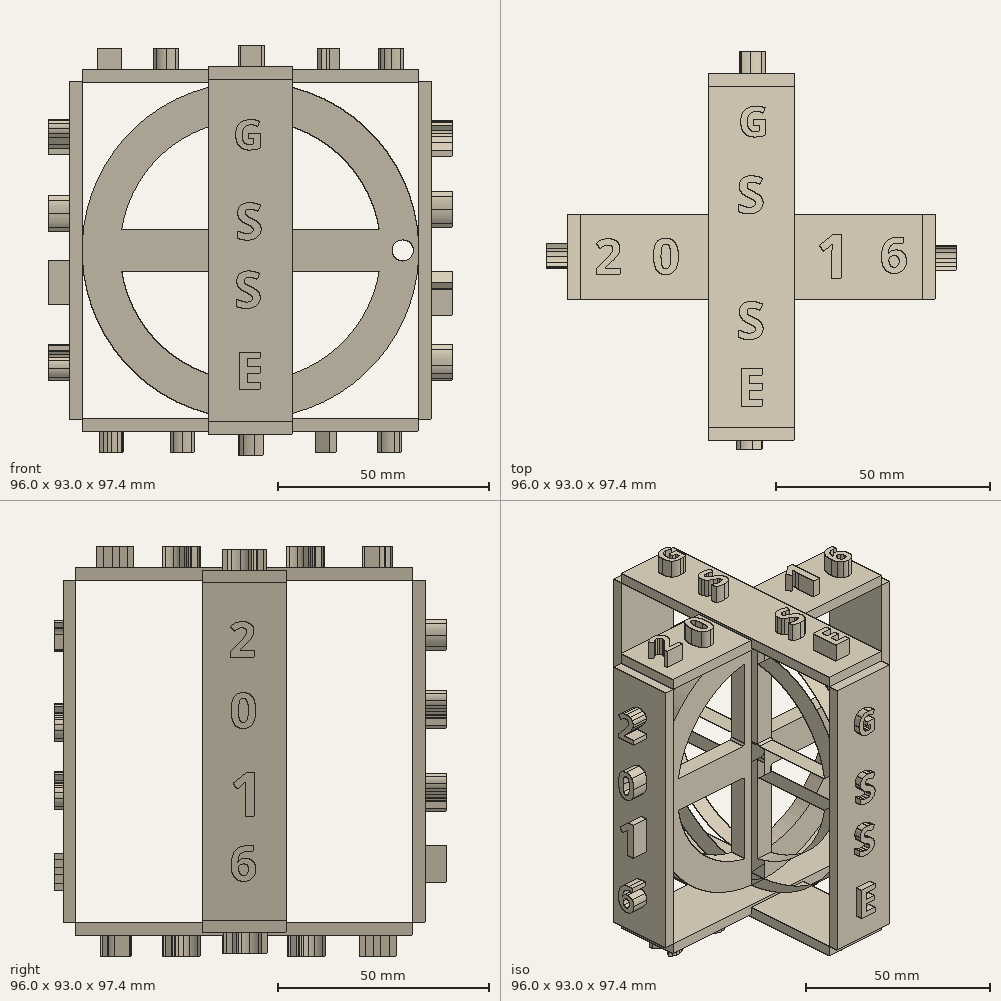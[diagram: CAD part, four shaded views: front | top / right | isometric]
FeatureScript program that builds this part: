
annotation { "Feature Type Name" : "Feature", "Feature Type Description" : "" }
export const myFeature = defineFeature(function(context is Context, id is Id, definition is map)
    precondition{}
    {
        {
            var Q0;
            Q0=qCreatedBy(makeId("Front.planeOp"),FACE);
            var sketch = newSketch(context, id + "F0", { "sketchPlane" : qUnion([Q0])});
            skArc(sketch, "E0", {"start": v(-30.6, -5) * mm, "mid": v(-21.92, -21.92) * mm, "end": v(-5, -30.6) * mm});
            skCircle(sketch, "E1", {"center": v(0, 0) * mm, "radius": 40 * mm});
            skArc(sketch, "E2", {"start": v(5, -5.6) * mm, "mid": v(5.3, -5.3) * mm, "end": v(5.6, -5) * mm});
            skCircle(sketch, "E3", {"center": v(0, 0) * mm, "radius": 2.5 * mm});
            skLineSegment(sketch, "E4", {"start": v(0, 0) * mm, "end": v(0, 31) * mm, "construction": true});
            skLineSegment(sketch, "E5", {"start": v(0, 0) * mm, "end": v(31, 0) * mm, "construction": true});
            skLineSegment(sketch, "E6", {"start": v(0, 0) * mm, "end": v(0, -31) * mm, "construction": true});
            skLineSegment(sketch, "E7", {"start": v(0, 0) * mm, "end": v(-31, 0) * mm, "construction": true});
            skLineSegment(sketch, "E8.0", {"start": v(5, 5.6) * mm, "end": v(5, 30.6) * mm});
            skLineSegment(sketch, "E9.0", {"start": v(-5, 5.6) * mm, "end": v(-5, 30.6) * mm});
            skLineSegment(sketch, "E10.0", {"start": v(-5.6, 5) * mm, "end": v(-30.6, 5) * mm});
            skLineSegment(sketch, "E11.0", {"start": v(-5.6, -5) * mm, "end": v(-30.6, -5) * mm});
            skLineSegment(sketch, "E12.0", {"start": v(-5, -5.6) * mm, "end": v(-5, -30.6) * mm});
            skLineSegment(sketch, "E13.0", {"start": v(5.6, -5) * mm, "end": v(30.6, -5) * mm});
            skLineSegment(sketch, "E14.0", {"start": v(5.6, 5) * mm, "end": v(30.6, 5) * mm});
            skArc(sketch, "E15.trimOffspring", {"start": v(30.6, 5) * mm, "mid": v(21.92, 21.92) * mm, "end": v(5, 30.6) * mm});
            skArc(sketch, "E16.trimOffspring", {"start": v(5.6, 5) * mm, "mid": v(5.3, 5.3) * mm, "end": v(5, 5.6) * mm});
            skArc(sketch, "E17.trimOffspring", {"start": v(-5.6, -5) * mm, "mid": v(-5.3, -5.3) * mm, "end": v(-5, -5.6) * mm});
            skArc(sketch, "E18.trimOffspring", {"start": v(-5, 5.6) * mm, "mid": v(-5.3, 5.3) * mm, "end": v(-5.6, 5) * mm});
            skLineSegment(sketch, "E19.trimOffspring", {"start": v(5, -5.6) * mm, "end": v(5, -30.6) * mm});
            skArc(sketch, "E20.trimOffspring", {"start": v(-5, 30.6) * mm, "mid": v(-21.92, 21.92) * mm, "end": v(-30.6, 5) * mm});
            skArc(sketch, "E21.trimOffspring", {"start": v(5, -30.6) * mm, "mid": v(21.92, -21.92) * mm, "end": v(30.6, -5) * mm});
            skCircle(sketch, "E22", {"center": v(36.2, 0) * mm, "radius": 2.5 * mm});
            skSolve(sketch);
        }
        {
            var Q0;
            Q0=makeQuery(id+"F0.imprint","IMPRINT",FACE,{"disambiguationData":[TD([[makeQuery(id+"F0.imprint","IMPRINT",EDGE,{"derivedFrom":sQuery(id+"F0.wireOp",EDGE,"E0")}),-1.0]])]});
            extrude(context, id + "F1", {"entities" : qUnion([Q0]), "endBound" : BoundingType.SYMMETRIC, "depth" : 5 * mm});
        }
        {
            var Q0;
            Q0=qCreatedBy(makeId("Right.planeOp"),FACE);
            var sketch = newSketch(context, id + "F2", { "sketchPlane" : qUnion([Q0])});
            skCircle(sketch, "E23", {"center": v(0, 0) * mm, "radius": 40 * mm});
            skArc(sketch, "E24", {"start": v(-30.6, -5) * mm, "mid": v(-21.92, -21.92) * mm, "end": v(-5, -30.6) * mm});
            skArc(sketch, "E25", {"start": v(-5, 5.6) * mm, "mid": v(-5.3, 5.3) * mm, "end": v(-5.6, 5) * mm});
            skCircle(sketch, "E26", {"center": v(0, 0) * mm, "radius": 2.5 * mm});
            skLineSegment(sketch, "E27", {"start": v(0, 0) * mm, "end": v(0, 31) * mm});
            skLineSegment(sketch, "E28", {"start": v(0, 0) * mm, "end": v(31, 0) * mm});
            skLineSegment(sketch, "E29", {"start": v(0, 0) * mm, "end": v(0, -31) * mm});
            skLineSegment(sketch, "E30", {"start": v(0, 0) * mm, "end": v(-31, 0) * mm});
            skLineSegment(sketch, "E31.0", {"start": v(5, 5.6) * mm, "end": v(5, 30.6) * mm});
            skLineSegment(sketch, "E32.0", {"start": v(-5, 5.6) * mm, "end": v(-5, 30.6) * mm});
            skLineSegment(sketch, "E33.0", {"start": v(5.6, -5) * mm, "end": v(30.6, -5) * mm});
            skLineSegment(sketch, "E34.0", {"start": v(5.6, 5) * mm, "end": v(30.6, 5) * mm});
            skLineSegment(sketch, "E35.0", {"start": v(-5, -5.6) * mm, "end": v(-5, -30.6) * mm});
            skLineSegment(sketch, "E36.0", {"start": v(5, -5.6) * mm, "end": v(5, -30.6) * mm});
            skLineSegment(sketch, "E37.0", {"start": v(-5.6, 5) * mm, "end": v(-30.6, 5) * mm});
            skLineSegment(sketch, "E38.0", {"start": v(-5.6, -5) * mm, "end": v(-30.6, -5) * mm});
            skArc(sketch, "E39.trimOffspring", {"start": v(5, -30.6) * mm, "mid": v(21.92, -21.92) * mm, "end": v(30.6, -5) * mm});
            skArc(sketch, "E40.trimOffspring", {"start": v(-5, 30.6) * mm, "mid": v(-21.92, 21.92) * mm, "end": v(-30.6, 5) * mm});
            skArc(sketch, "E41.trimOffspring", {"start": v(30.6, 5) * mm, "mid": v(21.92, 21.92) * mm, "end": v(5, 30.6) * mm});
            skArc(sketch, "E42.trimOffspring", {"start": v(5.6, 5) * mm, "mid": v(5.3, 5.3) * mm, "end": v(5, 5.6) * mm});
            skArc(sketch, "E43.trimOffspring", {"start": v(5, -5.6) * mm, "mid": v(5.3, -5.3) * mm, "end": v(5.6, -5) * mm});
            skArc(sketch, "E44.trimOffspring", {"start": v(-5.6, -5) * mm, "mid": v(-5.3, -5.3) * mm, "end": v(-5, -5.6) * mm});
            skSolve(sketch);
        }
        {
            var Q0;
            Q0=makeQuery(id+"F2.imprint","IMPRINT",FACE,{"disambiguationData":[TD([[makeQuery(id+"F2.imprint","IMPRINT",EDGE,{"derivedFrom":sQuery(id+"F2.wireOp",EDGE,"E23")}),1.0]])]});
            extrude(context, id + "F3", {"entities" : qUnion([Q0]), "operationType" : NewBodyOperationType.ADD, "endBound" : BoundingType.SYMMETRIC, "depth" : 5 * mm});
        }
        {
            var Q0;
            Q0=qCreatedBy(makeId("Right.planeOp"),FACE);
            var sketch = newSketch(context, id + "F4", { "sketchPlane" : qUnion([Q0])});
            skLineSegment(sketch, "E45.bottom", {"start": v(40.01, -40.7) * mm, "end": v(-40.02, -40.7) * mm});
            skLineSegment(sketch, "E45.top", {"start": v(40.02, 40.7) * mm, "end": v(-40.02, 40.7) * mm});
            skLineSegment(sketch, "E45.left", {"start": v(40.02, -40.7) * mm, "end": v(40.02, 40.7) * mm});
            skLineSegment(sketch, "E45.right", {"start": v(-40.02, -40.7) * mm, "end": v(-40.02, 40.7) * mm});
            skPoint(sketch, "E45.middle", {"position": v(0, 0) * mm});
            skPoint(sketch, "E46.visualSharp", {"position": v(-40.02, 40.7) * mm});
            skLineSegment(sketch, "E46.filletArc", {"start": v(-40.02, 40.7) * mm, "end": v(-40.02, 40.7) * mm});
            skPoint(sketch, "E47.visualSharp", {"position": v(40.02, 40.7) * mm});
            skLineSegment(sketch, "E47.filletArc", {"start": v(40.02, 40.7) * mm, "end": v(40.02, 40.7) * mm});
            skPoint(sketch, "E48.visualSharp", {"position": v(-40.02, -40.7) * mm});
            skLineSegment(sketch, "E48.filletArc", {"start": v(-40.02, -40.7) * mm, "end": v(-40.02, -40.7) * mm});
            skPoint(sketch, "E49.visualSharp", {"position": v(40.02, -40.7) * mm});
            skLineSegment(sketch, "E49.filletArc", {"start": v(40.02, -40.7) * mm, "end": v(40.02, -40.7) * mm});
            skSolve(sketch);
        }
        {
            var Q0;
            Q0=makeQuery(id+"F4.imprint","IMPRINT",FACE,{"disambiguationData":[TD([[makeQuery(id+"F4.imprint","IMPRINT",EDGE,{"derivedFrom":sQuery(id+"F4.wireOp",EDGE,"E45.bottom")}),-1.0]])]});
            var Q1;
            Q1=sQuery(id+"F4.wireOp",EDGE,"E45.top");
            var Q2;
            Q2=sQuery(id+"F4.wireOp",EDGE,"E45.left");
            var Q3;
            Q3=sQuery(id+"F4.wireOp",EDGE,"E45.bottom");
            var Q4;
            Q4=sQuery(id+"F4.wireOp",EDGE,"E45.right");
            extrude(context, id + "F5", {"entities" : qUnion([Q0]), "bodyType" : ToolBodyType.SURFACE, "surfaceEntities" : qUnion([Q1, Q2, Q3, Q4]), "endBound" : BoundingType.SYMMETRIC, "depth" : 20 * mm});
        }
        {
            var Q0;
            Q0=qCreatedBy(makeId("Front.planeOp"),FACE);
            var sketch = newSketch(context, id + "F6", { "sketchPlane" : qUnion([Q0])});
            skLineSegment(sketch, "E50.bottom", {"start": v(-40, 40.02) * mm, "end": v(40.01, 40.02) * mm});
            skLineSegment(sketch, "E50.top", {"start": v(-40.01, -40.02) * mm, "end": v(40, -40.02) * mm});
            skLineSegment(sketch, "E50.left", {"start": v(-40, 40.02) * mm, "end": v(-40.01, -40.03) * mm});
            skLineSegment(sketch, "E50.right", {"start": v(40.01, 40.02) * mm, "end": v(40, -40.03) * mm});
            skPoint(sketch, "E50.middle", {"position": v(0, 0) * mm});
            skSolve(sketch);
        }
        {
            var Q0;
            Q0=sQuery(id+"F6.wireOp",EDGE,"E50.bottom");
            var Q1;
            Q1=sQuery(id+"F6.wireOp",EDGE,"E50.right");
            var Q2;
            Q2=sQuery(id+"F6.wireOp",EDGE,"E50.top");
            var Q3;
            Q3=sQuery(id+"F6.wireOp",EDGE,"E50.left");
            extrude(context, id + "F7", {"bodyType" : ToolBodyType.SURFACE, "surfaceEntities" : qUnion([Q0, Q1, Q2, Q3]), "endBound" : BoundingType.SYMMETRIC, "depth" : 20 * mm});
        }
        {
            var Q0;
            Q0=makeQuery(id+"F5.opExtrude","SWEPT_FACE",FACE,{"disambiguationData":[OSD([sQuery(id+"F4.wireOp",EDGE,"E45.right")])]});
            var sketch = newSketch(context, id + "F8", { "sketchPlane" : qUnion([Q0])});
            skText(sketch, "E51", { "text": "G", "fontName": "OpenSans-Bold.ttf"});
            skText(sketch, "E52", { "text": "S", "fontName": "OpenSans-Bold.ttf"});
            skText(sketch, "E53", { "text": "S", "fontName": "OpenSans-Bold.ttf"});
            skText(sketch, "E54", { "text": "E", "fontName": "OpenSans-Bold.ttf"});
            const initialGuessF8  = {"E51": [-0.00408, 0.02395, 1, 0, 0.0071], "E52": [-0.00369, 0.00256, 1, 0, 0.00875], "E53": [-0.00391, -0.01366, 1, 0, 0.00875], "E54": [-0.0037, -0.033, 1, 0, 0.0089]};
            skSetInitialGuess(sketch, initialGuessF8);
            skSolve(sketch);
        }
        {
            var Q0;
            Q0 = qSketchRegion(id + "F8", true);
            extrude(context, id + "F9", {"entities" : qUnion([Q0]), "depth" : 5 * mm});
        }
        {
            var Q0;
            Q0=makeQuery(id+"F5.opExtrude","SWEPT_FACE",FACE,{"disambiguationData":[OSD([sQuery(id+"F4.wireOp",EDGE,"E45.right")])]});
            extrude(context, id + "F10", {"entities" : qUnion([Q0]), "depth" : 3 * mm});
        }
        {
            var Q0;
            Q0=makeQuery(id+"F5.opExtrude","SWEPT_FACE",FACE,{"disambiguationData":[OSD([sQuery(id+"F4.wireOp",EDGE,"E45.top")])]});
            extrude(context, id + "F11", {"entities" : qUnion([Q0]), "depth" : 3 * mm});
        }
        {
            var Q0;
            Q0=makeQuery(id+"F5.opExtrude","SWEPT_FACE",FACE,{"disambiguationData":[OSD([sQuery(id+"F4.wireOp",EDGE,"E45.left")])]});
            extrude(context, id + "F12", {"entities" : qUnion([Q0]), "depth" : 3 * mm});
        }
        {
            var Q0;
            Q0=makeQuery(id+"F5.opExtrude","SWEPT_FACE",FACE,{"disambiguationData":[OSD([sQuery(id+"F4.wireOp",EDGE,"E45.bottom")])]});
            extrude(context, id + "F13", {"entities" : qUnion([Q0]), "depth" : 3 * mm});
        }
        {
            var Q0;
            Q0=makeQuery(id+"F7.opExtrude","SWEPT_FACE",FACE,{"disambiguationData":[OSD([sQuery(id+"F6.wireOp",EDGE,"E50.bottom")])]});
            extrude(context, id + "F14", {"entities" : qUnion([Q0]), "operationType" : NewBodyOperationType.ADD, "oppositeDirection" : true, "depth" : 3 * mm});
        }
        {
            var Q0;
            Q0=makeQuery(id+"F7.opExtrude","SWEPT_FACE",FACE,{"disambiguationData":[OSD([sQuery(id+"F6.wireOp",EDGE,"E50.right")])]});
            extrude(context, id + "F15", {"entities" : qUnion([Q0]), "oppositeDirection" : true, "depth" : 3 * mm});
        }
        {
            var Q0;
            Q0=makeQuery(id+"F7.opExtrude","SWEPT_FACE",FACE,{"disambiguationData":[OSD([sQuery(id+"F6.wireOp",EDGE,"E50.top")])]});
            extrude(context, id + "F16", {"entities" : qUnion([Q0]), "operationType" : NewBodyOperationType.ADD, "oppositeDirection" : true, "depth" : 3 * mm});
        }
        {
            var Q0;
            Q0=makeQuery(id+"F7.opExtrude","SWEPT_FACE",FACE,{"disambiguationData":[OSD([sQuery(id+"F6.wireOp",EDGE,"E50.left")])]});
            extrude(context, id + "F17", {"entities" : qUnion([Q0]), "oppositeDirection" : true, "depth" : 3 * mm});
        }
        {
            var Q0;
            Q0=makeQuery(id+"F17.opExtrude","CAP_FACE",FACE,{"disambiguationData":[OSD([sQuery(id+"F6.wireOp",EDGE,"E50.left")])],"isStart":false});
            var sketch = newSketch(context, id + "F18", { "sketchPlane" : qUnion([Q0])});
            skText(sketch, "E55", { "text": "2", "fontName": "OpenSans-Bold.ttf"});
            skText(sketch, "E56", { "text": "0", "fontName": "OpenSans-Bold.ttf"});
            skText(sketch, "E57", { "text": "1", "fontName": "OpenSans-Bold.ttf"});
            skText(sketch, "E58", { "text": "6", "fontName": "OpenSans-Bold.ttf"});
            const initialGuessF18  = {"E55": [-0.0035, 0.02273, 1, 0, 0.00835], "E56": [-0.0035, 0.00454, 1, 0, 0.0084], "E57": [-0.0035, -0.01293, 1, 0, 0.01054], "E58": [-0.0035, -0.03075, 1, 0, 0.00835]};
            skSetInitialGuess(sketch, initialGuessF18);
            skSolve(sketch);
        }
        {
            var Q0;
            Q0 = qSketchRegion(id + "F18", true);
            extrude(context, id + "F19", {"entities" : qUnion([Q0]), "operationType" : NewBodyOperationType.ADD, "depth" : 5 * mm});
        }
        {
            var Q0;
            Q0=makeQuery(id+"F15.opExtrude","CAP_FACE",FACE,{"disambiguationData":[OSD([sQuery(id+"F6.wireOp",EDGE,"E50.right")])],"isStart":false});
            var sketch = newSketch(context, id + "F20", { "sketchPlane" : qUnion([Q0])});
            skText(sketch, "E59", { "text": "2", "fontName": "OpenSans-Bold.ttf"});
            skText(sketch, "E60", { "text": "0", "fontName": "OpenSans-Bold.ttf"});
            skText(sketch, "E61", { "text": "1", "fontName": "OpenSans-Bold.ttf"});
            skText(sketch, "E62", { "text": "6", "fontName": "OpenSans-Bold.ttf"});
            const initialGuessF20  = {"E59": [-0.0037, 0.02244, 1, 0, 0.00835], "E60": [-0.0035, 0.00553, 1, 0, 0.0084], "E61": [-0.0035, -0.01541, 1, 0, 0.01054], "E62": [-0.0035, -0.03075, 1, 0, 0.00835]};
            skSetInitialGuess(sketch, initialGuessF20);
            skSolve(sketch);
        }
        {
            var Q0;
            Q0 = qSketchRegion(id + "F20", true);
            extrude(context, id + "F21", {"entities" : qUnion([Q0]), "operationType" : NewBodyOperationType.ADD, "depth" : 5 * mm});
        }
        {
            var Q0;
            Q0=makeQuery(id+"F12.opExtrude","CAP_FACE",FACE,{"disambiguationData":[OSD([sQuery(id+"F4.wireOp",EDGE,"E45.left")])],"isStart":false});
            var sketch = newSketch(context, id + "F22", { "sketchPlane" : qUnion([Q0])});
            skText(sketch, "E63", { "text": "G", "fontName": "OpenSans-Bold.ttf"});
            skText(sketch, "E64", { "text": "S", "fontName": "OpenSans-Bold.ttf"});
            skText(sketch, "E65", { "text": "S", "fontName": "OpenSans-Bold.ttf"});
            skText(sketch, "E66", { "text": "E", "fontName": "OpenSans-Bold.ttf"});
            const initialGuessF22  = {"E63": [-0.0039, 0.02412, 1, 0, 0.0071], "E64": [-0.0035, 0.00569, 1, 0, 0.00875], "E65": [-0.0035, -0.01405, 1, 0, 0.00875], "E66": [-0.0035, -0.03115, 1, 0, 0.0089]};
            skSetInitialGuess(sketch, initialGuessF22);
            skSolve(sketch);
        }
        {
            var Q0;
            Q0 = qSketchRegion(id + "F22", true);
            extrude(context, id + "F23", {"entities" : qUnion([Q0]), "operationType" : NewBodyOperationType.ADD, "depth" : 5 * mm});
        }
        {
            var Q0;
            Q0=makeQuery(id+"F13.opExtrude","CAP_FACE",FACE,{"disambiguationData":[OSD([sQuery(id+"F4.wireOp",EDGE,"E45.bottom")])],"isStart":false});
            var sketch = newSketch(context, id + "F24", { "sketchPlane" : qUnion([Q0])});
            skText(sketch, "E67", { "text": "G", "fontName": "OpenSans-Bold.ttf"});
            skText(sketch, "E68", { "text": "S", "fontName": "OpenSans-Bold.ttf"});
            skText(sketch, "E69", { "text": "S", "fontName": "OpenSans-Bold.ttf"});
            skText(sketch, "E70", { "text": "E", "fontName": "OpenSans-Bold.ttf"});
            const initialGuessF24  = {"E67": [-0.00323, 0.0269, 1, 0, 0.0071], "E68": [-0.0035, 0.0106, 1, 0, 0.00875], "E69": [-0.0035, -0.01919, 1, 0, 0.00875], "E70": [-0.0035, -0.0361, 1, 0, 0.0089]};
            skSetInitialGuess(sketch, initialGuessF24);
            skSolve(sketch);
        }
        {
            var Q0;
            Q0 = qSketchRegion(id + "F24", true);
            extrude(context, id + "F25", {"entities" : qUnion([Q0]), "operationType" : NewBodyOperationType.ADD, "depth" : 5 * mm});
        }
        {
            var Q0;
            Q0=makeQuery(id+"F11.opExtrude","CAP_FACE",FACE,{"disambiguationData":[OSD([sQuery(id+"F4.wireOp",EDGE,"E45.top")])],"isStart":false});
            var sketch = newSketch(context, id + "F26", { "sketchPlane" : qUnion([Q0])});
            skText(sketch, "E71", { "text": "G", "fontName": "OpenSans-Bold.ttf"});
            skText(sketch, "E72", { "text": "S", "fontName": "OpenSans-Bold.ttf"});
            skText(sketch, "E73", { "text": "S", "fontName": "OpenSans-Bold.ttf"});
            skText(sketch, "E74", { "text": "E", "fontName": "OpenSans-Bold.ttf"});
            const initialGuessF26  = {"E71": [-0.00309, 0.02816, 1, 0, 0.0071], "E72": [-0.0035, 0.0102, 1, 0, 0.00875], "E73": [-0.0035, -0.01926, 1, 0, 0.00875], "E74": [-0.0035, -0.035, 1, 0, 0.0089]};
            skSetInitialGuess(sketch, initialGuessF26);
            skSolve(sketch);
        }
        {
            var Q0;
            Q0 = qSketchRegion(id + "F26", true);
            extrude(context, id + "F27", {"entities" : qUnion([Q0]), "operationType" : NewBodyOperationType.ADD, "depth" : 5 * mm});
        }
        {
            var Q0;
            {var subQ1=sQuery(id+"F6.wireOp",EDGE,"E50.top");Q0=makeQuery(id+"F16.boolean.opBoolean","SPLIT",FACE,{"disambiguationData":[TD([makeQuery(id+"F16.opExtrude","SWEPT_FACE",FACE,{"disambiguationData":[OSD([sQuery(id+"F6.wireOp",VERTEX,"E50.top.end")])]})])],"derivedFrom":makeQuery(id+"F16.opExtrude","CAP_FACE",FACE,{"disambiguationData":[OSD([subQ1])],"isStart":false})});}
            var sketch = newSketch(context, id + "F28", { "sketchPlane" : qUnion([Q0])});
            skText(sketch, "E75", { "text": "2", "fontName": "OpenSans-Bold.ttf"});
            skText(sketch, "E76", { "text": "0", "fontName": "OpenSans-Bold.ttf"});
            skText(sketch, "E77", { "text": "1", "fontName": "OpenSans-Bold.ttf"});
            skText(sketch, "E78", { "text": "6", "fontName": "OpenSans-Bold.ttf"});
            const initialGuessF28  = {"E75": [-0.03638, -0.00327, 1, 0, 0.00835], "E76": [-0.01947, -0.00379, 1, 0, 0.0084], "E77": [0.01448, -0.00562, 1, 0, 0.01054], "E78": [0.0297, -0.00407, 1, 0, 0.00835]};
            skSetInitialGuess(sketch, initialGuessF28);
            skSolve(sketch);
        }
        {
            var Q0;
            Q0 = qSketchRegion(id + "F28", true);
            extrude(context, id + "F29", {"entities" : qUnion([Q0]), "operationType" : NewBodyOperationType.ADD, "depth" : 5 * mm});
        }
        {
            var Q0;
            Q0=makeQuery(id+"F14.opExtrude","CAP_FACE",FACE,{"disambiguationData":[OSD([sQuery(id+"F6.wireOp",EDGE,"E50.bottom")])],"isStart":false});
            var sketch = newSketch(context, id + "F30", { "sketchPlane" : qUnion([Q0])});
            skText(sketch, "E79", { "text": "2", "fontName": "OpenSans-Bold.ttf"});
            skText(sketch, "E80", { "text": "0", "fontName": "OpenSans-Bold.ttf"});
            skText(sketch, "E81", { "text": "1", "fontName": "OpenSans-Bold.ttf"});
            skText(sketch, "E82", { "text": "6", "fontName": "OpenSans-Bold.ttf"});
            const initialGuessF30  = {"E79": [-0.03682, -0.00415, 1, 0, 0.00835], "E80": [-0.02337, -0.00408, 1, 0, 0.0084], "E81": [0.015, -0.00517, 1, 0, 0.01054], "E82": [0.03004, -0.00375, 1, 0, 0.00835]};
            skSetInitialGuess(sketch, initialGuessF30);
            skSolve(sketch);
        }
        {
            var Q0;
            Q0 = qSketchRegion(id + "F30", true);
            extrude(context, id + "F31", {"entities" : qUnion([Q0]), "operationType" : NewBodyOperationType.ADD, "depth" : 5 * mm});
        }
    });
